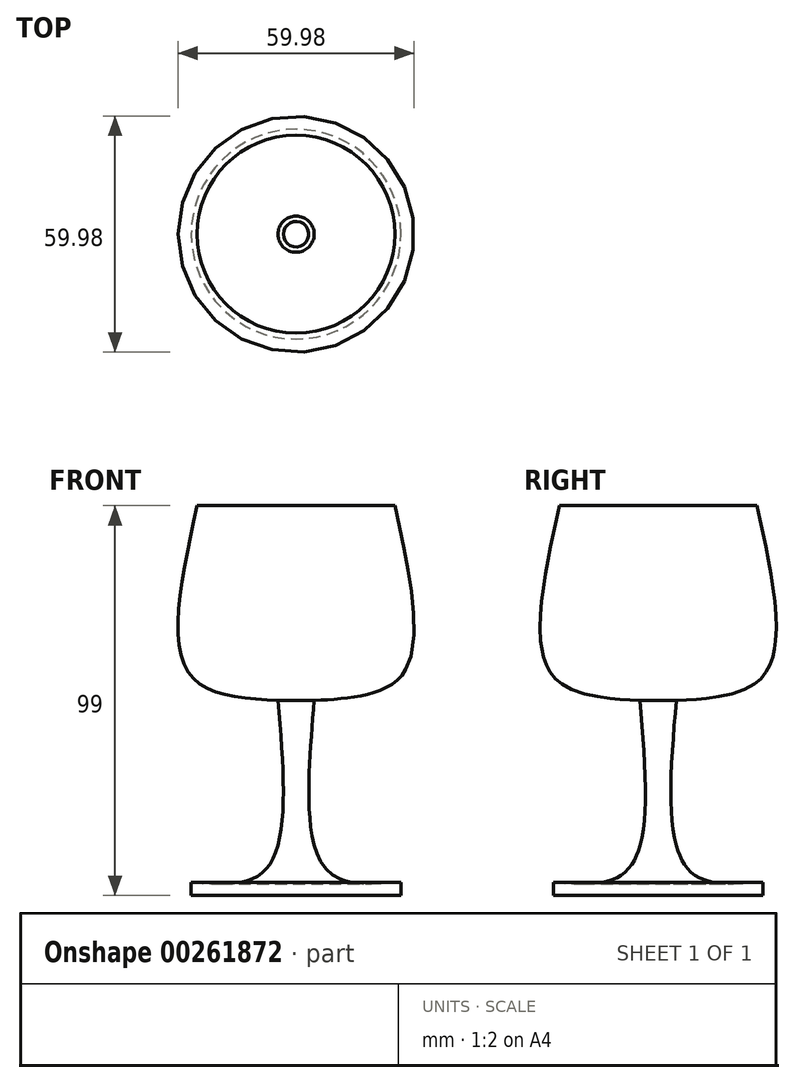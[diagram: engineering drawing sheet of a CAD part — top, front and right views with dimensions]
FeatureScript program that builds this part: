
annotation { "Feature Type Name" : "Feature", "Feature Type Description" : "" }
export const myFeature = defineFeature(function(context is Context, id is Id, definition is map)
    precondition{}
    {
        {
            var Q0;
            Q0=qCreatedBy(makeId("Front.planeOp"),FACE);
            var sketch = newSketch(context, id + "F0", { "sketchPlane" : qUnion([Q0])});
            skLineSegment(sketch, "E0", {"start": v(0, 251.37) * mm, "end": v(0, -256.63) * mm, "construction": true});
            skSolve(sketch);
        }
        {
            var Q0;
            Q0=qCreatedBy(makeId("Front.planeOp"),FACE);
            var sketch = newSketch(context, id + "F1", { "sketchPlane" : qUnion([Q0])});
            skFitSpline(sketch, "E1", {"points": [v(0, -56.44) * mm, v(-26.64, -56.44) * mm], "startDerivative": vector(-26.64, 0) * mm, "endDerivative": vector(-26.64, 0) * mm});
            skLineSegment(sketch, "E2", {"start": v(-26.64, -56.44) * mm, "end": v(-26.64, -53.12) * mm});
            skFitSpline(sketch, "E3", {"points": [v(-26.64, -53.12) * mm, v(-7.62, -49.8) * mm, v(-4.6, -6.94) * mm], "startDerivative": vector(55.88, -4.43) * mm, "endDerivative": vector(-7.63, 90.54) * mm});
            skFitSpline(sketch, "E4", {"points": [v(-4.6, -6.94) * mm, v(-27.24, 0) * mm, v(-25.13, 42.56) * mm], "startDerivative": vector(-65.1, 3.86) * mm, "endDerivative": vector(19.93, 90.9) * mm});
            skLineSegment(sketch, "E5", {"start": v(-25.13, 42.56) * mm, "end": v(0, 42.56) * mm});
            skSolve(sketch);
        }
        {
            var Q0;
            Q0 = qSketchRegion(id + "F1", true);
            var Q1;
            Q1=sQuery(id+"F1.wireOp",EDGE,"E4");
            var Q2;
            Q2=sQuery(id+"F1.wireOp",EDGE,"E3");
            var Q3;
            Q3=sQuery(id+"F1.wireOp",EDGE,"E1");
            var Q4;
            Q4=sQuery(id+"F1.wireOp",EDGE,"E2");
            var Q5;
            Q5=sQuery(id+"F0.wireOp",EDGE,"E0");
            revolve(context, id + "F2", {"bodyType" : ToolBodyType.SURFACE, "operationType" : NewBodyOperationType.ADD, "entities" : qUnion([Q0]), "surfaceEntities" : qUnion([Q1, Q2, Q3, Q4]), "axis" : qUnion([Q5]), "revolveType" : RevolveType.FULL});
        }
    });
